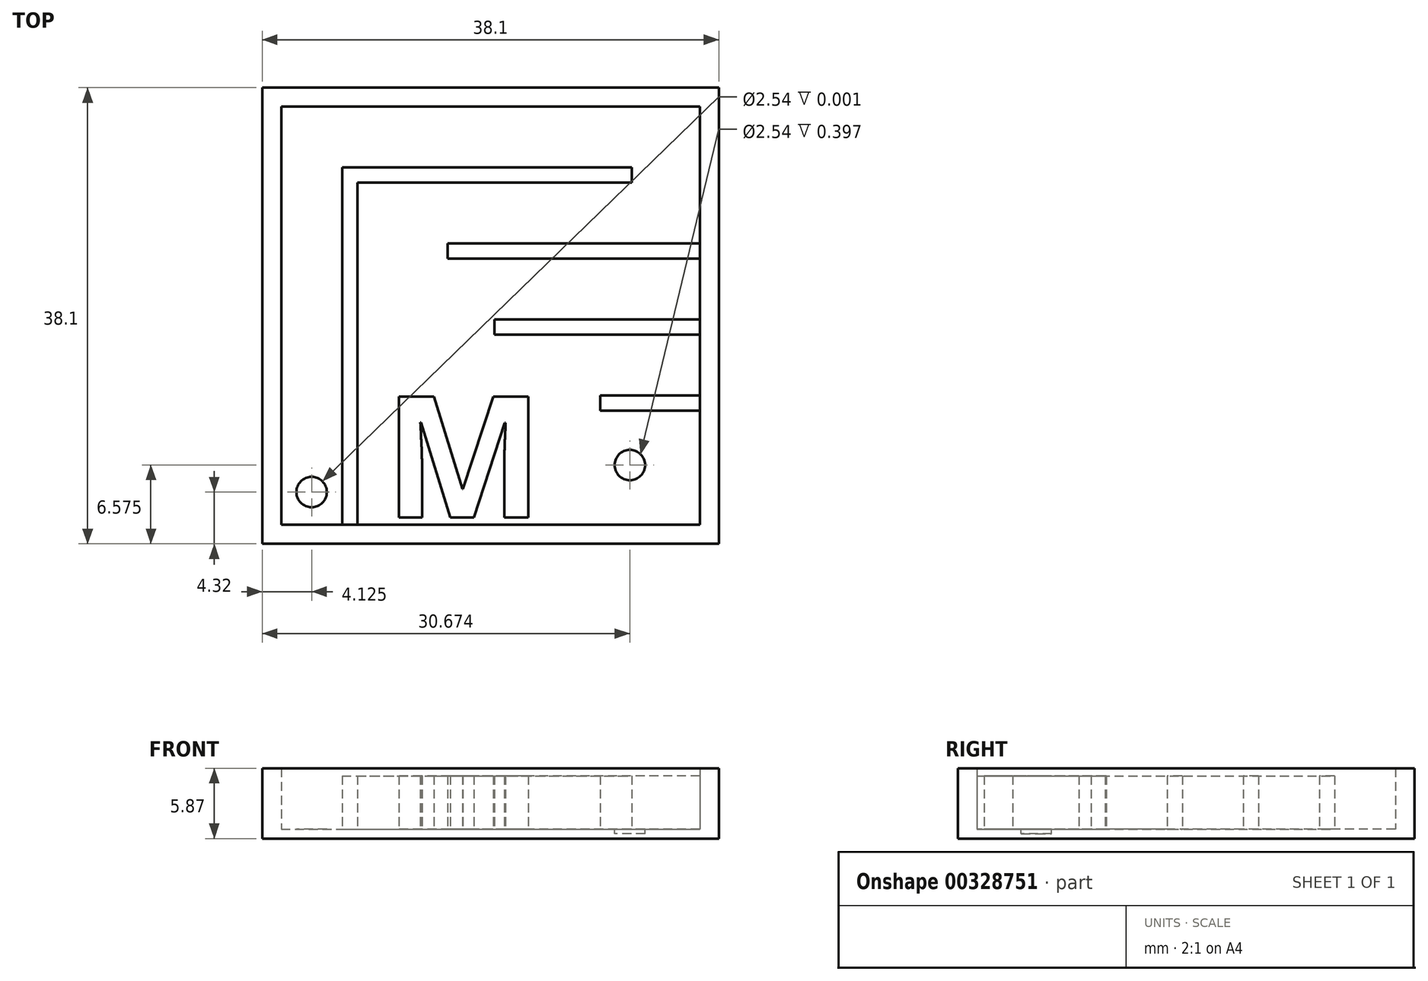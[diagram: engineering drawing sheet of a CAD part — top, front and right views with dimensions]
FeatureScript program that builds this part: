
annotation { "Feature Type Name" : "Feature", "Feature Type Description" : "" }
export const myFeature = defineFeature(function(context is Context, id is Id, definition is map)
    precondition{}
    {
        {
            var Q0;
            Q0=qCreatedBy(makeId("Top.planeOp"),FACE);
            var sketch = newSketch(context, id + "F0", { "sketchPlane" : qUnion([Q0])});
            skLineSegment(sketch, "E0.bottom", {"start": v(-17.2, 23.46) * mm, "end": v(20.9, 23.46) * mm});
            skLineSegment(sketch, "E0.top", {"start": v(-17.2, -14.64) * mm, "end": v(20.9, -14.64) * mm});
            skLineSegment(sketch, "E0.left", {"start": v(-17.2, 23.46) * mm, "end": v(-17.2, -14.64) * mm});
            skLineSegment(sketch, "E0.right", {"start": v(20.9, 23.46) * mm, "end": v(20.9, -14.64) * mm});
            skSolve(sketch);
        }
        {
            var Q0;
            Q0=makeQuery(id+"F0.imprint","IMPRINT",FACE,{"disambiguationData":[TD([[makeQuery(id+"F0.imprint","IMPRINT",EDGE,{"derivedFrom":sQuery(id+"F0.wireOp",EDGE,"E0.bottom")}),-1.0]])]});
            extrude(context, id + "F1", {"entities" : qUnion([Q0]), "depth" : 0.8 * mm});
        }
        {
            var Q0;
            Q0=makeQuery(id+"F1.opExtrude","CAP_FACE",FACE,{"disambiguationData":[OSD([sQuery(id+"F0.wireOp",EDGE,"E0.bottom"),sQuery(id+"F0.wireOp",EDGE,"E0.top"),sQuery(id+"F0.wireOp",EDGE,"E0.left"),sQuery(id+"F0.wireOp",EDGE,"E0.right")])],"isStart":false});
            var sketch = newSketch(context, id + "F2", { "sketchPlane" : qUnion([Q0])});
            skLineSegment(sketch, "E1.0", {"start": v(-15.6, 21.88) * mm, "end": v(19.32, 21.88) * mm});
            skLineSegment(sketch, "E1.1", {"start": v(-15.6, 21.88) * mm, "end": v(-15.6, -13.05) * mm});
            skLineSegment(sketch, "E1.2", {"start": v(-15.6, -13.05) * mm, "end": v(19.32, -13.05) * mm});
            skLineSegment(sketch, "E1.3", {"start": v(19.32, 21.88) * mm, "end": v(19.32, -13.05) * mm});
            skSolve(sketch);
        }
        {
            var Q0;
            Q0=makeQuery(id+"F2.imprint","IMPRINT",FACE,{"disambiguationData":[TD([[makeQuery(id+"F2.imprint","IMPRINT",EDGE,{"derivedFrom":sQuery(id+"F2.wireOp",EDGE,"E1.0")}),1.0]])]});
            extrude(context, id + "F3", {"entities" : qUnion([Q0]), "operationType" : NewBodyOperationType.ADD, "depth" : 5.08 * mm});
        }
        {
            var Q0;
            Q0=makeQuery(id+"F1.opExtrude","CAP_FACE",FACE,{"disambiguationData":[OSD([sQuery(id+"F0.wireOp",EDGE,"E0.bottom"),sQuery(id+"F0.wireOp",EDGE,"E0.top"),sQuery(id+"F0.wireOp",EDGE,"E0.left"),sQuery(id+"F0.wireOp",EDGE,"E0.right")])],"isStart":false});
            var sketch = newSketch(context, id + "F4", { "sketchPlane" : qUnion([Q0])});
            skLineSegment(sketch, "E2.bottom", {"start": v(-10.53, -13.05) * mm, "end": v(-9.26, -13.05) * mm});
            skLineSegment(sketch, "E2.top", {"start": v(-10.53, 16.8) * mm, "end": v(-9.26, 16.8) * mm});
            skLineSegment(sketch, "E2.left", {"start": v(-10.53, -13.05) * mm, "end": v(-10.53, 16.8) * mm});
            skLineSegment(sketch, "E2.right", {"start": v(-9.26, -13.05) * mm, "end": v(-9.26, -7.97) * mm});
            skLineSegment(sketch, "E3.bottom", {"start": v(-9.26, 16.8) * mm, "end": v(13.66, 16.8) * mm});
            skLineSegment(sketch, "E3.top", {"start": v(-9.26, 15.53) * mm, "end": v(13.66, 15.53) * mm});
            skLineSegment(sketch, "E3.right", {"start": v(13.66, 16.8) * mm, "end": v(13.66, 15.53) * mm});
            skLineSegment(sketch, "E4.left", {"start": v(-9.26, -3.45) * mm, "end": v(-9.26, -2.33) * mm});
            skLineSegment(sketch, "E5.trimOffspring", {"start": v(-9.26, -2.33) * mm, "end": v(-9.26, 15.53) * mm});
            skPoint(sketch, "E6.oppositeSnap0", {"position": v(2.2, 16.8) * mm});
            skLineSegment(sketch, "E7.left", {"start": v(-9.26, -7.94) * mm, "end": v(-9.26, -7.97) * mm});
            skPoint(sketch, "E6.right.end.orphan", {"position": v(2.2, 9.34) * mm});
            skPoint(sketch, "E7.right.end.orphan", {"position": v(13.66, -3.52) * mm});
            skLineSegment(sketch, "E8.trimOffspring", {"start": v(-9.26, -3.45) * mm, "end": v(-9.26, -2.25) * mm});
            skLineSegment(sketch, "E9.top", {"start": v(-2.37, -13.05) * mm, "end": v(-2.04, -13.05) * mm});
            skLineSegment(sketch, "E10.left", {"start": v(19.32, 10.45) * mm, "end": v(19.32, 9.37) * mm});
            skLineSegment(sketch, "E11.bottom", {"start": v(19.32, 2.83) * mm, "end": v(2.18, 2.83) * mm});
            skLineSegment(sketch, "E11.top", {"start": v(19.32, 4.1) * mm, "end": v(2.18, 4.1) * mm});
            skLineSegment(sketch, "E11.left", {"start": v(19.32, 2.83) * mm, "end": v(19.32, 4.1) * mm});
            skLineSegment(sketch, "E11.right", {"start": v(2.18, 2.83) * mm, "end": v(2.18, 4.1) * mm});
            skLineSegment(sketch, "E12.bottom", {"start": v(-9.26, -2.25) * mm, "end": v(-9.26, -2.25) * mm});
            skLineSegment(sketch, "E12.top", {"start": v(-9.26, -7.97) * mm, "end": v(-9.26, -7.97) * mm});
            skLineSegment(sketch, "E13.bottom", {"start": v(0, -13.05) * mm, "end": v(-2.04, -13.05) * mm});
            skLineSegment(sketch, "E14.left", {"start": v(19.32, -2.19) * mm, "end": v(19.32, -3.64) * mm});
            skLineSegment(sketch, "E15.bottom", {"start": v(8.7, -13.05) * mm, "end": v(11, -13.05) * mm});
            skLineSegment(sketch, "E16.bottom", {"start": v(19.32, -2.25) * mm, "end": v(11, -2.25) * mm});
            skLineSegment(sketch, "E16.top", {"start": v(19.32, -3.52) * mm, "end": v(11, -3.52) * mm});
            skLineSegment(sketch, "E16.left", {"start": v(19.32, -2.25) * mm, "end": v(19.32, -3.52) * mm});
            skLineSegment(sketch, "E16.right", {"start": v(11, -2.25) * mm, "end": v(11, -3.52) * mm});
            skLineSegment(sketch, "E17.bottom", {"start": v(19.32, 10.45) * mm, "end": v(-1.73, 10.45) * mm});
            skLineSegment(sketch, "E17.top", {"start": v(19.32, 9.18) * mm, "end": v(-1.73, 9.18) * mm});
            skLineSegment(sketch, "E17.left", {"start": v(19.32, 10.45) * mm, "end": v(19.32, 9.18) * mm});
            skLineSegment(sketch, "E17.right", {"start": v(-1.73, 10.45) * mm, "end": v(-1.73, 9.18) * mm});
            skLineSegment(sketch, "E18", {"start": v(-10.53, -13.05) * mm, "end": v(-15.6, -13.05) * mm});
            skCircle(sketch, "E19", {"center": v(-13.07, -10.32) * mm, "radius": 1.27 * mm});
            skPoint(sketch, "E19.centerSnap0", {"position": v(-13.07, -13.05) * mm});
            skLineSegment(sketch, "E20.left", {"start": v(-9.26, -3.45) * mm, "end": v(-9.26, -4.73) * mm});
            skLineSegment(sketch, "E21.left", {"start": v(-9.26, -7.97) * mm, "end": v(-9.26, -6.7) * mm});
            skLineSegment(sketch, "E21.right", {"start": v(6.5, -7.97) * mm, "end": v(6.5, -6.7) * mm});
            skLineSegment(sketch, "E22.trimOffspring", {"start": v(-9.26, -3.52) * mm, "end": v(-9.26, -6.7) * mm});
            skText(sketch, "E23", { "text": "M", "fontName": "OpenSans-Bold.ttf"});
            skCircle(sketch, "E24", {"center": v(13.48, -8.07) * mm, "radius": 1.27 * mm});
            const initialGuessF4  = {"E23": [-0.00704, -0.01243, 1, 0, 0.01017]};
            skSetInitialGuess(sketch, initialGuessF4);
            skSolve(sketch);
        }
        {
            var Q0;
            Q0=makeQuery(id+"F4.imprint","IMPRINT",FACE,{"disambiguationData":[TD([[makeQuery(id+"F4.imprint","IMPRINT",EDGE,{"derivedFrom":sQuery(id+"F4.wireOp",EDGE,"E2.bottom")}),1.0]])]});
            var Q1;
            {var subQ0=sQuery(id+"F4.wireOp",EDGE,"E17.bottom");Q1=makeQuery(id+"F4.imprint","IMPRINT",FACE,{"disambiguationData":[TD([[makeQuery(id+"F4.imprint","IMPRINT",EDGE,{"derivedFrom":subQ0}),1.0]])]});}
            var Q2;
            Q2=makeQuery(id+"F4.imprint","IMPRINT",FACE,{"disambiguationData":[TD([[makeQuery(id+"F4.imprint","IMPRINT",EDGE,{"derivedFrom":sQuery(id+"F4.wireOp",EDGE,"E11.bottom")}),-1.0]])]});
            var Q3;
            Q3=makeQuery(id+"F4.imprint","IMPRINT",FACE,{"disambiguationData":[TD([[makeQuery(id+"F4.imprint","IMPRINT",EDGE,{"derivedFrom":sQuery(id+"F4.wireOp",EDGE,"E16.bottom")}),1.0]])]});
            extrude(context, id + "F5", {"entities" : qUnion([Q0, Q1, Q2, Q3]), "operationType" : NewBodyOperationType.ADD, "depth" : 4.44 * mm});
        }
        {
            var Q0;
            Q0=makeQuery(id+"F4.imprint","IMPRINT",FACE,{"disambiguationData":[TD([[makeQuery(id+"F4.imprint","IMPRINT",EDGE,{"derivedFrom":sQuery(id+"F4.wireOp",EDGE,"E19")}),1.0]])]});
            extrude(context, id + "F6", {"entities" : qUnion([Q0]), "operationType" : NewBodyOperationType.REMOVE, "oppositeDirection" : true, "depth" : 1 / 1625.6 * mm});
        }
        {
            var Q0;
            Q0=makeQuery(id+"F4.imprint","IMPRINT",FACE,{"disambiguationData":[TD([[makeQuery(id+"F4.imprint","IMPRINT",EDGE,{"derivedFrom":sQuery(id+"F4.wireOp",EDGE,"E23.sketch_text.stroke-0")}),-1.0]])]});
            extrude(context, id + "F7", {"entities" : qUnion([Q0]), "operationType" : NewBodyOperationType.ADD, "depth" : 4.44 * mm});
        }
        {
            var Q0;
            Q0=makeQuery(id+"F4.imprint","IMPRINT",FACE,{"disambiguationData":[TD([[makeQuery(id+"F4.imprint","IMPRINT",EDGE,{"derivedFrom":sQuery(id+"F4.wireOp",EDGE,"E24")}),1.0]])]});
            extrude(context, id + "F8", {"entities" : qUnion([Q0]), "operationType" : NewBodyOperationType.REMOVE, "oppositeDirection" : true, "depth" : 0.4 * mm});
        }
    });
